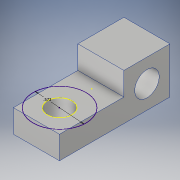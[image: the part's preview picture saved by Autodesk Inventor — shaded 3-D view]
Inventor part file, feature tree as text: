
AUTODESK INVENTOR PART (.ipt)
format: ipt  version: 2018 (Build 220112000, 112)  size: 154,112 bytes
history: native  units: in
note: dims shown in document units (in); Inventor stores cm internally (conversion verified against a paired STEP export)
features: sketch x5, extrude x2, hole x2, fillet x1
ambient origin geometry x8: Origin, YZ Plane, XZ Plane, XY Plane, X Axis, Y Axis, Z Axis, Center Point
bodies: Solid1 (feature_tree)
feature tree (10):
  extrude  "Extrusion1"  Depth=1.2in
  hole  "Hole1"  [1 undecoded]
  hole  "Hole2"  [1 undecoded]
  extrude  "Extrusion2"  Depth=0.25in
  sketch  "Sketch5"  dims[d15=0.266in d16=0.75in d17=0.507in d18=0.25in d19=0.5635in d20=1.0in d21=0.8108in d23=0.25in d24=0.5in d25=0.0in d26=0.573in d27=0.25in d28=0.5in d29=0.125in]
  fillet  "Fillet1"  Radius=0.5in
  sketch  "Sketch1"  dims[d0=0.5in d1=1.2in]
  sketch  "Sketch2"  dims[d2=0.5in d3=0.0in]
  sketch  "Sketch3"  dims[d5=0.266in d6=0.75in d7=0.507in d8=0.25in d9=0.5635in d10=1.0in d11=0.8108in d12=0.25in]
  sketch  "Sketch4"  dims[d13=0.25in d14=90.0deg]
note: 2 required parameter values undecoded (feature->parameter linkage not recoverable at this tier; creation-order binding heuristic only, values carry confidence <= 0.55)
